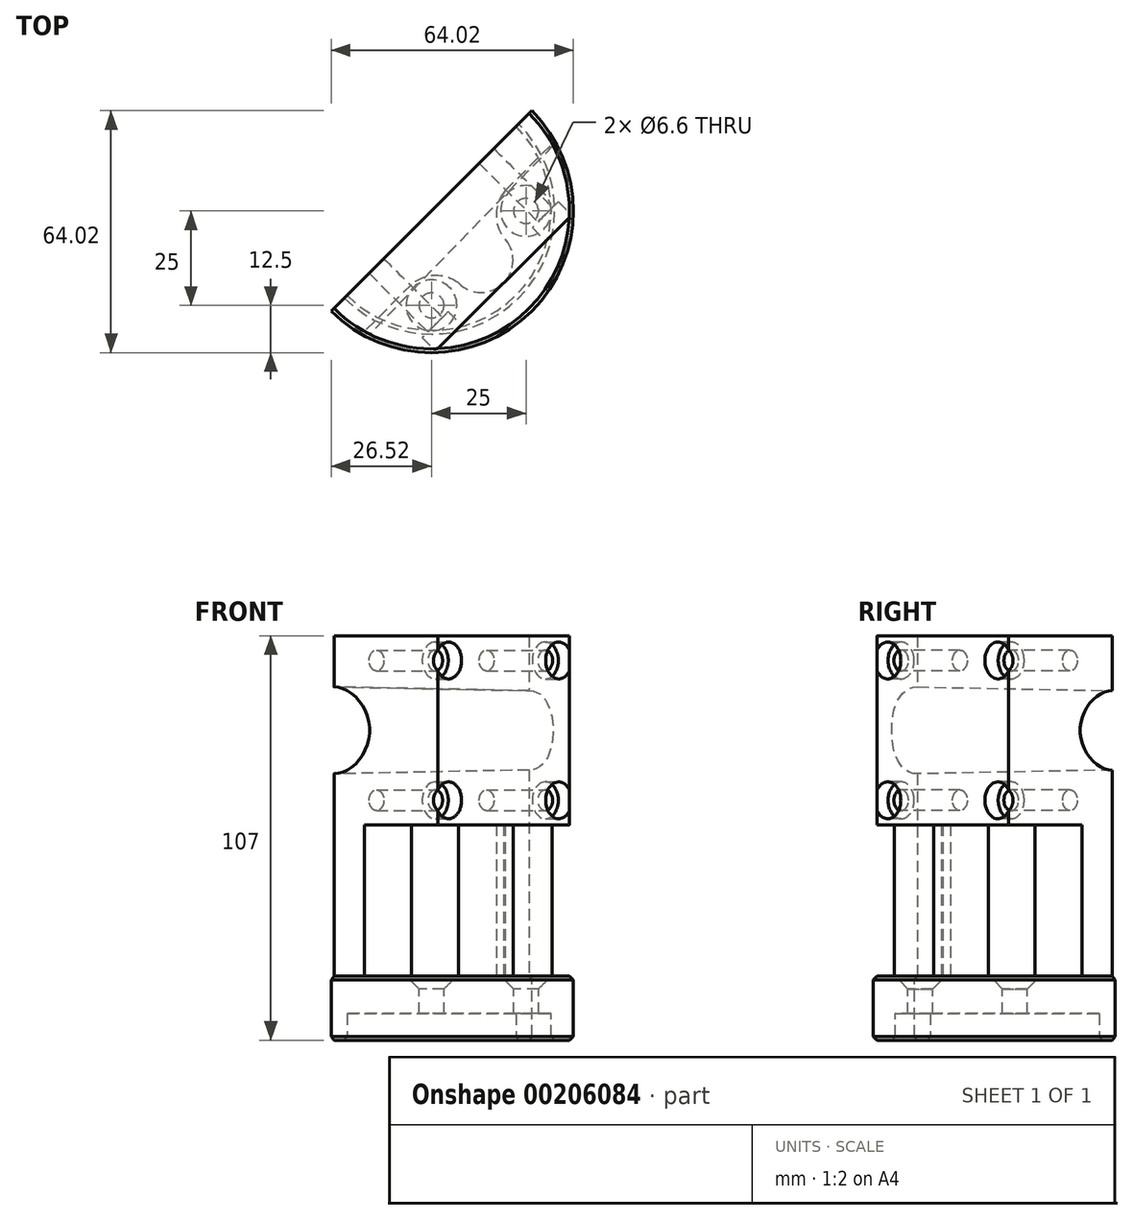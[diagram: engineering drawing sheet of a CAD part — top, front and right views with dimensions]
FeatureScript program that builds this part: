
annotation { "Feature Type Name" : "Feature", "Feature Type Description" : "" }
export const myFeature = defineFeature(function(context is Context, id is Id, definition is map)
    precondition{}
    {
        {
            var Q0;
            Q0=qCreatedBy(makeId("Front.planeOp"),FACE);
            var sketch = newSketch(context, id + "F0", { "sketchPlane" : qUnion([Q0])});
            skLineSegment(sketch, "E0", {"start": v(0, 0) * mm, "end": v(31.6, 0) * mm});
            skLineSegment(sketch, "E1", {"start": v(31.6, 0) * mm, "end": v(31.6, -7) * mm});
            skLineSegment(sketch, "E2", {"start": v(31.6, -7) * mm, "end": v(37.5, -7) * mm});
            skLineSegment(sketch, "E3", {"start": v(37.5, -7) * mm, "end": v(37.5, 10) * mm});
            skLineSegment(sketch, "E4", {"start": v(37.5, 10) * mm, "end": v(0, 10) * mm});
            skLineSegment(sketch, "E5", {"start": v(0, 10) * mm, "end": v(0, 0) * mm});
            skSolve(sketch);
        }
        {
            var Q0;
            Q0=qSketchRegion(id+"F0",true);
            var Q1;
            Q1=sQuery(id+"F0.wireOp",EDGE,"E5");
            revolve(context, id + "F1", {"entities" : qUnion([Q0]), "axis" : qUnion([Q1]), "revolveType" : RevolveType.TWO_DIRECTIONS, "angle" : 135 * degree, "angleBack" : 315 * degree});
        }
        {
            var Q0;
            Q0=makeQuery(id+"F1.opRevolve","SWEPT_EDGE",EDGE,{"disambiguationData":[OSD([sQuery(id+"F0.wireOp",EDGE,"E1"),sQuery(id+"F0.wireOp",EDGE,"E2")])]});
            var Q1;
            Q1=makeQuery(id+"F1.opRevolve","SWEPT_EDGE",EDGE,{"disambiguationData":[OSD([sQuery(id+"F0.wireOp",EDGE,"E2"),sQuery(id+"F0.wireOp",EDGE,"E3")])]});
            var Q2;
            Q2=makeQuery(id+"F1.opRevolve","SWEPT_EDGE",EDGE,{"disambiguationData":[OSD([sQuery(id+"F0.wireOp",EDGE,"E3"),sQuery(id+"F0.wireOp",EDGE,"E4")])]});
            chamfer(context, id + "F2", {"entities" : qUnion([Q0, Q1, Q2]), "width" : 1 * mm, "tangentPropagation" : true});
        }
        {
            var Q0;
            Q0=makeQuery(id+"F1.opRevolve","SWEPT_FACE",FACE,{"disambiguationData":[OSD([sQuery(id+"F0.wireOp",EDGE,"E4")])]});
            var sketch = newSketch(context, id + "F3", { "sketchPlane" : qUnion([Q0])});
            skCircle(sketch, "E6", {"center": v(0, 0) * mm, "radius": 25 * mm, "construction": true});
            skPoint(sketch, "E7", {"position": v(25, 0) * mm});
            skPoint(sketch, "E8", {"position": v(0, -25) * mm});
            skSolve(sketch);
        }
        {
            var Q0;
            Q0=sQuery(id+"F3.wireOp",VERTEX,"06cf2421-47d0-4dc6-992a-3eddbef67247");
            var Q1;
            Q1=sQuery(id+"F3.wireOp",VERTEX,"E7");
            var Q2;
            Q2=sQuery(id+"F3.wireOp",VERTEX,"E8");
            var Q3;
            Q3=sQuery(id+"F3.wireOp",VERTEX,"fbc0e9e7-8500-45a9-a549-826aceaf9aa4");
            var Q4;
            Q4=makeQuery(id+"F1.opRevolve","SWEPT_BODY",BODY,{"disambiguationData":[OSD([sQuery(id+"F0.wireOp",EDGE,"E0"),sQuery(id+"F0.wireOp",EDGE,"E1"),sQuery(id+"F0.wireOp",EDGE,"E2"),sQuery(id+"F0.wireOp",EDGE,"E3"),sQuery(id+"F0.wireOp",EDGE,"E4"),sQuery(id+"F0.wireOp",EDGE,"E5")])]});
            hole(context, id + "F4", {"style" : HoleStyle.C_SINK, "endStyle" : HoleEndStyle.THROUGH, "standardTappedOrClearance" : lookupTablePath({ "standard" : "ISO", "fit" : "Normal", "size" : "M6", "type" : "Clearance" }), "standardBlindInLast" : lookupTablePath({ "fit" : "Standard", "standard" : "ISO", "size" : "M6", "type" : "Clearance" }), "holeDiameter" : 6.6 * mm, "cSinkDiameter" : 13.44 * mm, "cSinkAngle" : 90 * degree, "locations" : qUnion([Q0, Q1, Q2, Q3]), "scope" : qUnion([Q4]), "isTappedThrough" : true});
        }
        {
            var Q0;
            Q0=makeQuery(id+"F1.opRevolve","SWEPT_FACE",FACE,{"disambiguationData":[OSD([sQuery(id+"F0.wireOp",EDGE,"E4")])]});
            var sketch = newSketch(context, id + "F5", { "sketchPlane" : qUnion([Q0])});
            skLineSegment(sketch, "E9", {"start": v(0, 0) * mm, "end": v(7.07, -7.07) * mm});
            skLineSegment(sketch, "E10", {"start": v(7.07, -7.07) * mm, "end": v(31.9, 17.75) * mm});
            skLineSegment(sketch, "E11", {"start": v(7.07, -7.07) * mm, "end": v(-17.75, -31.9) * mm});
            skLineSegment(sketch, "E12.bottom", {"start": v(7.07, -7.07) * mm, "end": v(19.07, -7.07) * mm, "construction": true});
            skLineSegment(sketch, "E12.top", {"start": v(7.07, -19.07) * mm, "end": v(19.07, -19.07) * mm, "construction": true});
            skLineSegment(sketch, "E12.left", {"start": v(7.07, -7.07) * mm, "end": v(7.07, -19.07) * mm, "construction": true});
            skLineSegment(sketch, "E12.right", {"start": v(19.07, -7.07) * mm, "end": v(19.07, -19.07) * mm, "construction": true});
            skArc(sketch, "E13", {"start": v(7.07, -19.07) * mm, "mid": v(0.8, -17.12) * mm, "end": v(-5.34, -19.48) * mm});
            skArc(sketch, "E14", {"start": v(19.48, 5.34) * mm, "mid": v(17.12, -0.8) * mm, "end": v(19.07, -7.07) * mm});
            skArc(sketch, "E15", {"start": v(7.07, -19.07) * mm, "mid": v(19.07, -19.07) * mm, "end": v(19.07, -7.07) * mm});
            skSolve(sketch);
        }
        {
            var Q0;
            Q0 = qSketchRegion(id + "F5", true);
            var Q1;
            {var subQ7=sQuery(id+"F5.wireOp",EDGE,"E9");Q1=makeQuery(id+"F5.imprint","IMPRINT",FACE,{"disambiguationData":[TD([[makeQuery(id+"F5.imprint","IMPRINT",EDGE,{"derivedFrom":subQ7}),-1.0]])]});}
            var Q2;
            {var subQ6=sQuery(id+"F5.wireOp",EDGE,"E9");Q2=makeQuery(id+"F5.imprint","IMPRINT",FACE,{"disambiguationData":[TD([[makeQuery(id+"F5.imprint","IMPRINT",EDGE,{"derivedFrom":subQ6}),1.0]])]});}
            extrude(context, id + "F6", {"entities" : qUnion([Q0, Q1, Q2]), "operationType" : NewBodyOperationType.ADD, "depth" : 40 * mm});
        }
        {
            var Q0;
            Q0=makeQuery(id+"F6.opExtrude","CAP_FACE",FACE,{"disambiguationData":[OSD([sQuery(id+"F0.wireOp",EDGE,"E3"),sQuery(id+"F0.wireOp",EDGE,"E4"),sQuery(id+"F5.wireOp",EDGE,"E10"),sQuery(id+"F5.wireOp",EDGE,"E11"),sQuery(id+"F5.wireOp",EDGE,"E13"),sQuery(id+"F5.wireOp",EDGE,"E14"),sQuery(id+"F5.wireOp",EDGE,"E15")])],"isStart":false});
            var sketch = newSketch(context, id + "F7", { "sketchPlane" : qUnion([Q0])});
            skArc(sketch, "E16", {"start": v(25.8, 25.8) * mm, "mid": v(25.8, -25.8) * mm, "end": v(-25.8, -25.8) * mm});
            skLineSegment(sketch, "E17", {"start": v(-25.8, -25.8) * mm, "end": v(25.8, 25.8) * mm});
            skLineSegment(sketch, "E18", {"start": v(19.07, -19.07) * mm, "end": v(36.46, -1.68) * mm});
            skLineSegment(sketch, "E19", {"start": v(36.46, -1.68) * mm, "end": v(1.68, -36.46) * mm});
            skSolve(sketch);
        }
        {
            var Q0;
            {var subQ1=makeQuery(id+"F6.opExtrude","CAP_EDGE",EDGE,{"disambiguationData":[OSD([sQuery(id+"F5.wireOp",EDGE,"E10")])],"isStart":false});Q0=makeQuery(id+"F7.imprint","IMPRINT",FACE,{"disambiguationData":[TD([[makeQuery(id+"F7.imprint","IMPRINT",EDGE,{"derivedFrom":subQ1}),-1.0]])]});}
            var Q1;
            {var subQ1=makeQuery(id+"F6.opExtrude","CAP_EDGE",EDGE,{"disambiguationData":[OSD([sQuery(id+"F5.wireOp",EDGE,"E11")])],"isStart":false});Q1=makeQuery(id+"F7.imprint","IMPRINT",FACE,{"disambiguationData":[TD([[makeQuery(id+"F7.imprint","IMPRINT",EDGE,{"derivedFrom":subQ1}),1.0]])]});}
            var Q2;
            {var subQ0=sQuery(id+"F7.wireOp",EDGE,"E17");Q2=makeQuery(id+"F7.imprint","IMPRINT",FACE,{"disambiguationData":[TD([[makeQuery(id+"F7.imprint","IMPRINT",EDGE,{"derivedFrom":subQ0}),-1.0]])]});}
            extrude(context, id + "F8", {"entities" : qUnion([Q0, Q1, Q2]), "operationType" : NewBodyOperationType.ADD, "depth" : 50 * mm});
        }
        {
            var Q0;
            {var subQ0=sQuery(id+"F0.wireOp",EDGE,"E4");Q0=makeQuery(id+"F8.boolean.opBoolean","MERGE",FACE,{"derivedFrom":[makeQuery(id+"F6.boolean.opBoolean","MERGE",FACE,{"derivedFrom":[makeQuery(id+"F1.opRevolve","CAP_FACE",FACE,{"disambiguationData":[OSD([sQuery(id+"F0.wireOp",EDGE,"E0"),sQuery(id+"F0.wireOp",EDGE,"E1"),sQuery(id+"F0.wireOp",EDGE,"E2"),sQuery(id+"F0.wireOp",EDGE,"E3"),subQ0,sQuery(id+"F0.wireOp",EDGE,"E5")])],"isStart":true}),makeQuery(id+"F6.opExtrude","SWEPT_FACE",FACE,{"disambiguationData":[OSD([subQ0])]})]}),makeQuery(id+"F8.opExtrude","SWEPT_FACE",FACE,{"disambiguationData":[OSD([sQuery(id+"F7.wireOp",EDGE,"E17")])]})]});}
            var sketch = newSketch(context, id + "F9", { "sketchPlane" : qUnion([Q0])});
            skLineSegment(sketch, "E20", {"start": v(-36.5, 100) * mm, "end": v(-36.5, 85.5) * mm, "construction": true});
            skLineSegment(sketch, "E21", {"start": v(36.5, 100) * mm, "end": v(36.5, 86.5) * mm, "construction": true});
            skLineSegment(sketch, "E22", {"start": v(-36.5, 85.5) * mm, "end": v(-36.5, 64.5) * mm, "construction": true});
            skLineSegment(sketch, "E23", {"start": v(36.5, 86.5) * mm, "end": v(36.5, 63.5) * mm, "construction": true});
            skLineSegment(sketch, "E24", {"start": v(-36.5, 85.5) * mm, "end": v(36.5, 86.5) * mm});
            skLineSegment(sketch, "E25", {"start": v(36.5, 86.5) * mm, "end": v(36.5, 63.5) * mm});
            skLineSegment(sketch, "E26", {"start": v(36.5, 63.5) * mm, "end": v(-36.5, 64.5) * mm});
            skLineSegment(sketch, "E27", {"start": v(-36.5, 64.5) * mm, "end": v(-36.5, 85.5) * mm});
            skLineSegment(sketch, "E28", {"start": v(-36.5, 75) * mm, "end": v(36.5, 75) * mm});
            skSolve(sketch);
        }
        {
            var Q0;
            {var subQ0=sQuery(id+"F9.wireOp",EDGE,"E24");Q0=makeQuery(id+"F9.imprint","IMPRINT",FACE,{"disambiguationData":[TD([[makeQuery(id+"F9.imprint","IMPRINT",EDGE,{"derivedFrom":subQ0}),-1.0]])]});}
            var Q1;
            Q1=sQuery(id+"F9.wireOp",EDGE,"E28");
            revolve(context, id + "F10", {"operationType" : NewBodyOperationType.REMOVE, "entities" : qUnion([Q0]), "axis" : qUnion([Q1]), "revolveType" : RevolveType.FULL, "oppositeDirection" : true});
        }
        {
            var Q0;
            Q0=makeQuery(id+"F8.opExtrude","SWEPT_FACE",FACE,{"disambiguationData":[OSD([sQuery(id+"F7.wireOp",EDGE,"E19")])]});
            var sketch = newSketch(context, id + "F11", { "sketchPlane" : qUnion([Q0])});
            skLineSegment(sketch, "E29", {"start": v(24.6, 100) * mm, "end": v(24.6, 93.5) * mm, "construction": true});
            skLineSegment(sketch, "E30", {"start": v(24.6, 93.5) * mm, "end": v(20.6, 93.5) * mm, "construction": true});
            skLineSegment(sketch, "E31", {"start": v(-24.6, 100) * mm, "end": v(-24.6, 93.5) * mm, "construction": true});
            skLineSegment(sketch, "E32", {"start": v(-24.6, 93.5) * mm, "end": v(-20.6, 93.5) * mm, "construction": true});
            skLineSegment(sketch, "E33", {"start": v(-24.6, 50) * mm, "end": v(-24.6, 56.5) * mm, "construction": true});
            skLineSegment(sketch, "E34", {"start": v(-24.6, 56.5) * mm, "end": v(-20.6, 56.5) * mm, "construction": true});
            skLineSegment(sketch, "E35", {"start": v(24.6, 50) * mm, "end": v(24.6, 56.5) * mm, "construction": true});
            skLineSegment(sketch, "E36", {"start": v(24.6, 56.5) * mm, "end": v(20.6, 56.5) * mm, "construction": true});
            skPoint(sketch, "E37", {"position": v(-20.6, 93.5) * mm});
            skPoint(sketch, "E38", {"position": v(20.6, 93.5) * mm});
            skPoint(sketch, "E39", {"position": v(20.6, 56.5) * mm});
            skPoint(sketch, "E40", {"position": v(-20.6, 56.5) * mm});
            skSolve(sketch);
        }
        {
            var Q0;
            Q0=sQuery(id+"F11.wireOp",VERTEX,"E38");
            var Q1;
            Q1=sQuery(id+"F11.wireOp",VERTEX,"E39");
            var Q2;
            Q2=sQuery(id+"F11.wireOp",VERTEX,"E40");
            var Q3;
            Q3=sQuery(id+"F11.wireOp",VERTEX,"E37");
            var Q4;
            Q4=makeQuery(id+"F1.opRevolve","SWEPT_BODY",BODY,{"disambiguationData":[OSD([sQuery(id+"F0.wireOp",EDGE,"E0"),sQuery(id+"F0.wireOp",EDGE,"E1"),sQuery(id+"F0.wireOp",EDGE,"E2"),sQuery(id+"F0.wireOp",EDGE,"E3"),sQuery(id+"F0.wireOp",EDGE,"E4"),sQuery(id+"F0.wireOp",EDGE,"E5")])]});
            hole(context, id + "F12", {"style" : HoleStyle.C_BORE, "endStyle" : HoleEndStyle.THROUGH, "standardTappedOrClearance" : lookupTablePath({ "standard" : "ISO", "fit" : "Normal", "size" : "M5", "type" : "Clearance" }), "standardBlindInLast" : lookupTablePath({ "fit" : "Standard", "standard" : "ISO", "size" : "M5", "type" : "Clearance" }), "holeDiameter" : 5.5 * mm, "cBoreDiameter" : 9.75 * mm, "cBoreDepth" : 5 * mm, "startFromSketch" : true, "locations" : qUnion([Q0, Q1, Q2, Q3]), "scope" : qUnion([Q4]), "isTappedThrough" : true});
        }
    });
